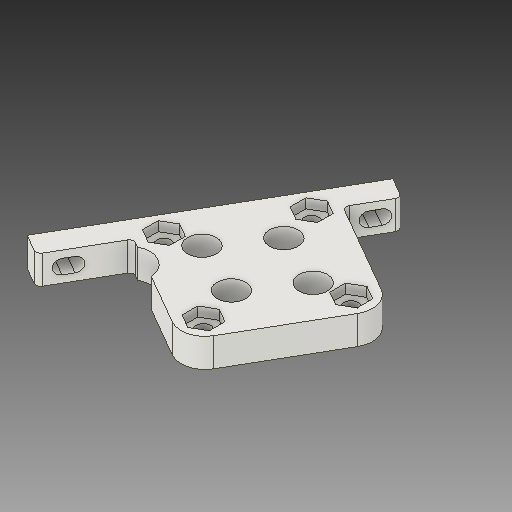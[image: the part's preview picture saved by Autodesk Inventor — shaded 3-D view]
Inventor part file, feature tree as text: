
AUTODESK INVENTOR PART (.ipt)
format: ipt  version: 2019 (Build 230136000, 136)  size: 160,768 bytes
history: imported  units: mm
features: imported_body x1
ambient origin geometry x8: Origin, YZ Plane, XZ Plane, XY Plane, X Axis, Y Axis, Z Axis, Center Point
bodies: Solide1 (imported_parasolid), Body3 (imported_parasolid)
feature tree (1):
  imported_body  NMx_Import_Brep_tag  [imported B-rep: ~62 faces, bbox_mm=[48.712813, 6.0, 50.497423]]
